# Revit family: Partition-Urinal_Screen-Bradley_Corp-St_Stl
name_source: partatom
category: Specialty Equipment
revit_build: Autodesk Revit MEP 2012 (Build: 20110309_2315(x64)
units: mm (PartAtom-declared; Revit-internal decimal feet)

## types (6) — shared parameters
ADA Compliant = No
Assembly Code = C1010400
Buy American Act = To Be Determined
Description = Restroom Partitions, Urinal Screen
Hardware Material = Metal - Bradley Corp - Chrome
Manufacturer = Bradley Corporation
MasterFormat Number = 10 21 13
MasterFormat Title = Toilet Compartments
Material = Stainless Steel
Material Note = Stainless Steel Hardware Also Available - Please See www.bradleycorp.com
Model = Stainless Steel - Urinal Screen
OmniClass Table 21 Number = 21-03 10 90 40
OmniClass Table 21 Title = Toilet, Bath, and Laundry Accessories
OmniClass Table 23 Number = 23.15.11.15.11
OmniClass Table 23 Title = Toilet Compartment and Urinal Screens
Product Tech Data URL - English = http://bradleycorp.com
Specifications URL = http://www.bradleycorp.com
URL = http://www.bradleycorp.com
Version = 2.0
Warranty Information = Warranted 15 years against rust out, 5 years on chrome hardware, lifetime of the partition on the stainless steel hardware.
zero-valued in all types: Percentage of Recycled Content

## per-type parameters (varying)
| type | Bracket Offset | Height | Width |
| 11" x 42" Urinal Screen | 1/2" | 42" | 11" |
| 17" x 42" Urinal Screen | 1/2" | 42" | 17" |
| 23" x 42" Urinal Screen | 1/2" | 42" | 23" |
| 11" x 48" Urinal Screen | 3 1/2" | 48" | 11" |
| 17" x 48" Urinal Screen | 3 1/2" | 48" | 17" |
| 23" x 48" Urinal Screen | 3 1/2" | 48" | 23" |

## geometry (parser evidence)
native form markers: Blend x8, Sweep x6
no freeform markers — native parametric forms only
